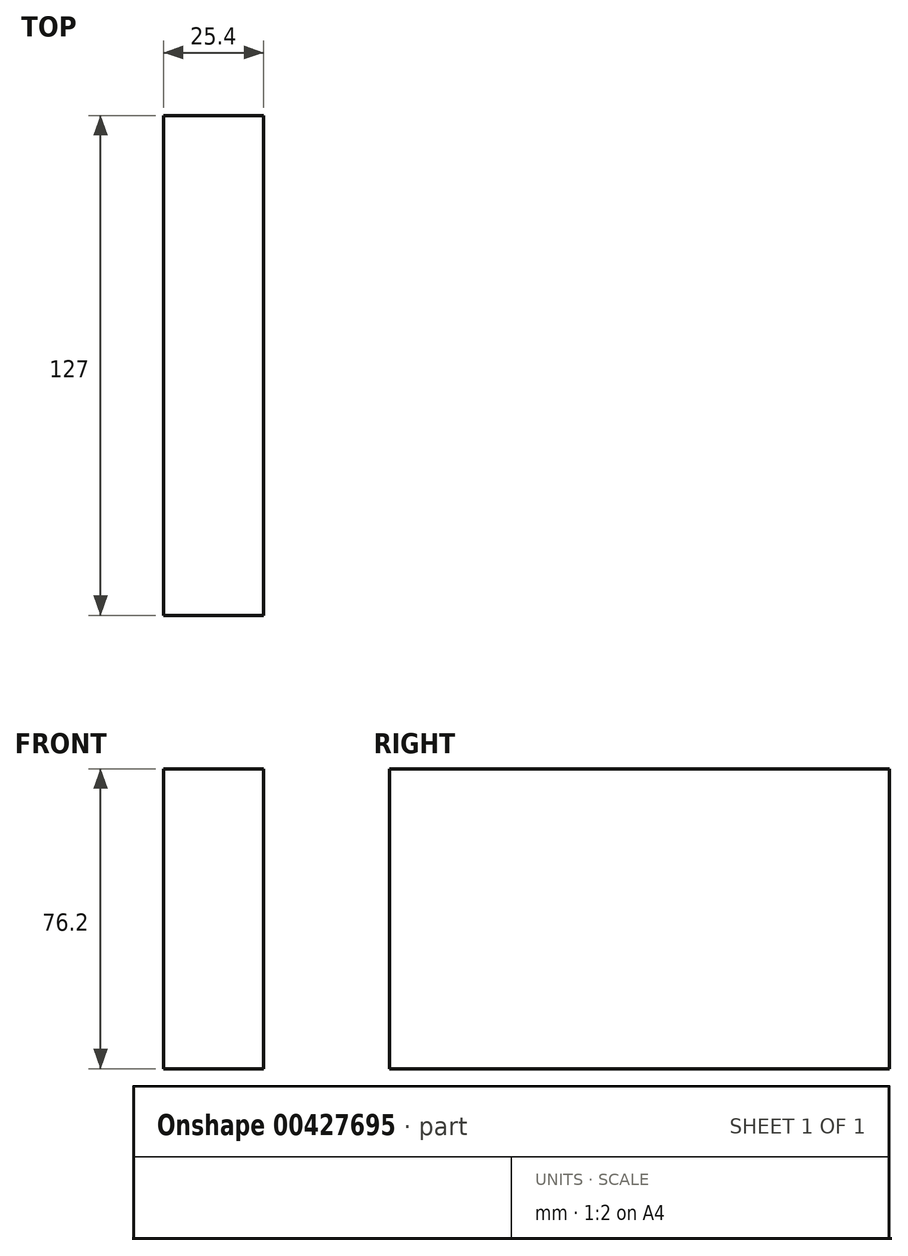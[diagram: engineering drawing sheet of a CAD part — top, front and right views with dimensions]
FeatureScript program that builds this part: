
annotation { "Feature Type Name" : "Feature", "Feature Type Description" : "" }
export const myFeature = defineFeature(function(context is Context, id is Id, definition is map)
    precondition{}
    {
        {
            var Q0;
            Q0=qCreatedBy(makeId("Right.planeOp"),FACE);
            var sketch = newSketch(context, id + "F0", { "sketchPlane" : qUnion([Q0])});
            skLineSegment(sketch, "E0.bottom", {"start": v(63.5, -38.1) * mm, "end": v(-63.5, -38.1) * mm});
            skLineSegment(sketch, "E0.top", {"start": v(63.5, 38.1) * mm, "end": v(-63.5, 38.1) * mm});
            skLineSegment(sketch, "E0.left", {"start": v(63.5, -38.1) * mm, "end": v(63.5, 38.1) * mm});
            skLineSegment(sketch, "E0.right", {"start": v(-63.5, -38.1) * mm, "end": v(-63.5, 38.1) * mm});
            skPoint(sketch, "E0.middle", {"position": v(0, 0) * mm});
            skSolve(sketch);
        }
        {
            var Q0;
            Q0 = qSketchRegion(id + "F0", true);
            extrude(context, id + "F1", {"entities" : qUnion([Q0]), "depth" : 25.4 * mm});
        }
    });
